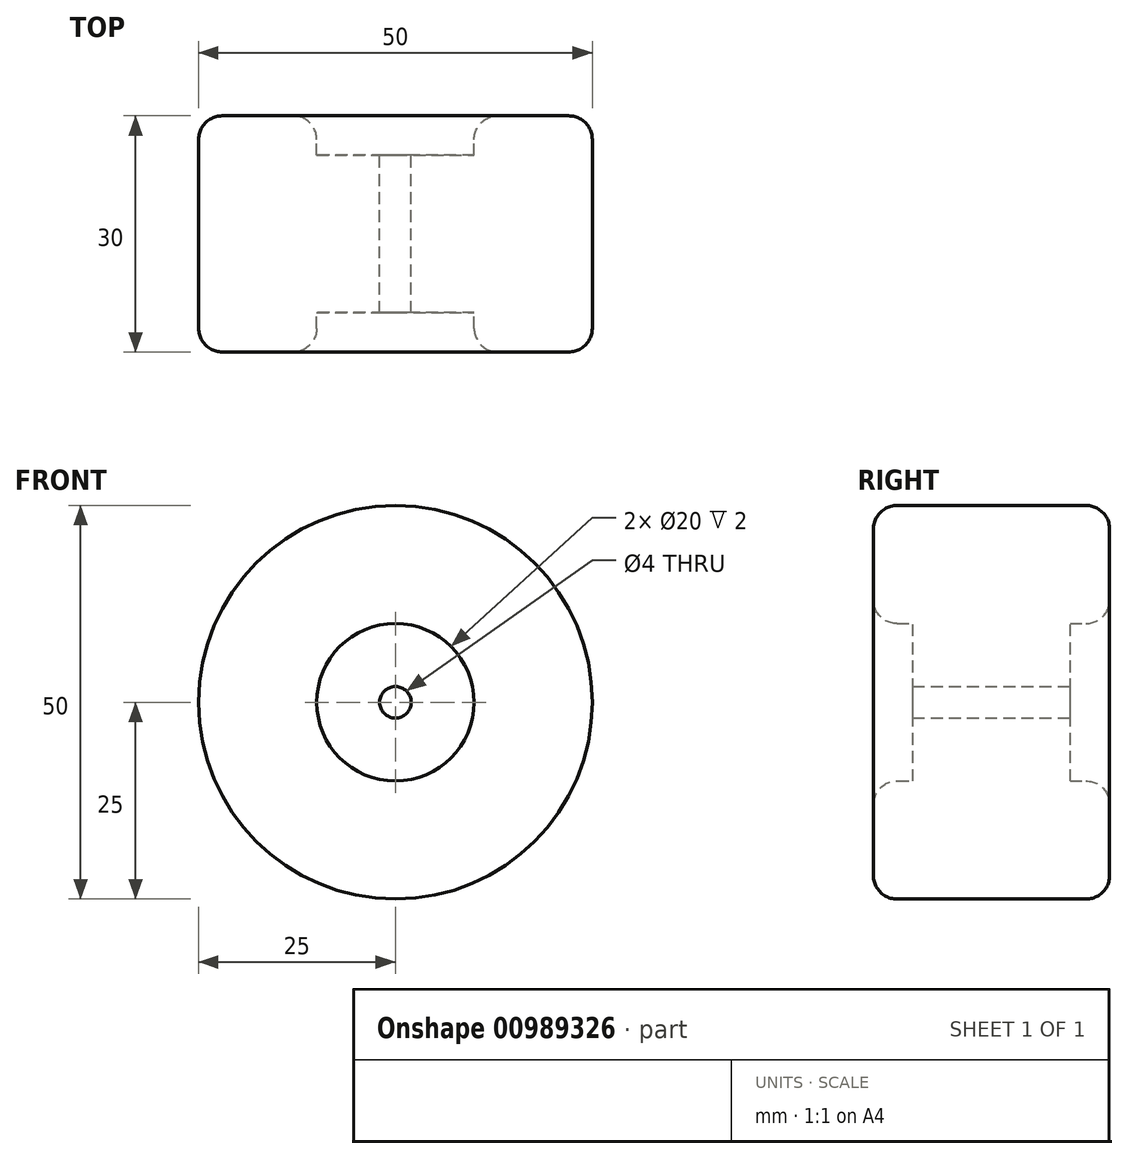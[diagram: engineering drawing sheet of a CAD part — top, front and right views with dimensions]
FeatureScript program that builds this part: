
annotation { "Feature Type Name" : "Feature", "Feature Type Description" : "" }
export const myFeature = defineFeature(function(context is Context, id is Id, definition is map)
    precondition{}
    {
        {
            var Q0;
            Q0=qCreatedBy(makeId("Front.planeOp"),FACE);
            var sketch = newSketch(context, id + "F0", { "sketchPlane" : qUnion([Q0])});
            skCircle(sketch, "E0", {"center": v(0, 0) * mm, "radius": 25 * mm});
            skCircle(sketch, "E1", {"center": v(0, 0) * mm, "radius": 10 * mm});
            skCircle(sketch, "E2", {"center": v(0, 0) * mm, "radius": 2 * mm});
            skSolve(sketch);
        }
        {
            var Q0;
            Q0=qSketchRegion(id+"F0",true);
            extrude(context, id + "F1", {"entities" : qUnion([Q0]), "depth" : 15 * mm, "offsetDistance" : 25 * mm, "hasSecondDirection" : true, "secondDirectionOppositeDirection" : true, "secondDirectionDepth" : 15 * mm});
        }
        {
            var Q0;
            Q0=makeQuery(id+"F0.imprint","IMPRINT",FACE,{"disambiguationData":[TD([[makeQuery(id+"F0.imprint","IMPRINT",EDGE,{"derivedFrom":sQuery(id+"F0.wireOp",EDGE,"E1")}),1.0]])]});
            extrude(context, id + "F2", {"entities" : qUnion([Q0]), "operationType" : NewBodyOperationType.ADD, "depth" : 10 * mm, "offsetDistance" : 25 * mm, "hasSecondDirection" : true, "secondDirectionOppositeDirection" : true, "secondDirectionDepth" : 10 * mm});
        }
        {
            var Q0;
            Q0=makeQuery(id+"F1.opExtrude","CAP_EDGE",EDGE,{"disambiguationData":[OSD([sQuery(id+"F0.wireOp",EDGE,"E0")])],"isStart":true});
            var Q1;
            Q1=makeQuery(id+"F1.opExtrude","CAP_EDGE",EDGE,{"disambiguationData":[OSD([sQuery(id+"F0.wireOp",EDGE,"E0")])],"isStart":false});
            var Q2;
            Q2=makeQuery(id+"F1.opExtrude","CAP_EDGE",EDGE,{"disambiguationData":[OSD([sQuery(id+"F0.wireOp",EDGE,"E1")])],"isStart":false});
            var Q3;
            Q3=makeQuery(id+"F1.opExtrude","CAP_EDGE",EDGE,{"disambiguationData":[OSD([sQuery(id+"F0.wireOp",EDGE,"E1")])],"isStart":true});
            fillet(context, id + "F3", {"entities" : qUnion([Q0, Q1, Q2, Q3]), "radius" : 3 * mm, "tangentPropagation" : true, "allowEdgeOverflow" : false});
        }
    });
